# Revit family: StructuralRoofDeck_NewMillennium_N-Dek
name_source: partatom
category: Generic Models
units: mm (PartAtom-declared; Revit-internal decimal feet)

## family parameters
Always vertical = Yes
Can host rebar = No
Classification Number = 23.25.30.27.14.14
Cut with Voids When Loaded = No
Maintain Annotation Orientation = No
Part Type = Normal
Room Calculation Point = No
Round Connector Dimension = Use Diameter
Shared = No
Work Plane-Based = No

## types (1)
- StructuralRoofDeck_NewMillennium_N-Dek
    Assembly Code = B1020260
    Building Codes = https://www.newmill.com
    Construction Details = https://www.newmill.com
    Cover Width = 2' - 0 1/2"
    Default Elevation = 0' - 0"
    Description = New Millennium Building Systems Roof Deck - N Dek
    Green Building-LEED = http://www.arcat.com
    Installation-Fabrication = https://www.newmill.com
    Keynote = 05 31 00
    Manufacturer = New Millennium Building Systems
    Manufacturer Fax = 260-868-6002
    Manufacturer Website = https://www.newmill.com
    Model = Roof Deck - N Dek
    Overall Depth = 0' - 3 1/16"
    Overall Length = 8' - 0"
    Panel Material = Steel as Specified
    Product Data = http://www.arcat.com
    Revision = R0_10-2017
    Sales Information = https://www.newmill.com
    Specification = http://www.arcat.com
    Test Data = https://www.newmill.com
    URL = https://www.newmill.com

## geometry (parser evidence)
native form markers: Sweep x3
no freeform markers — native parametric forms only
